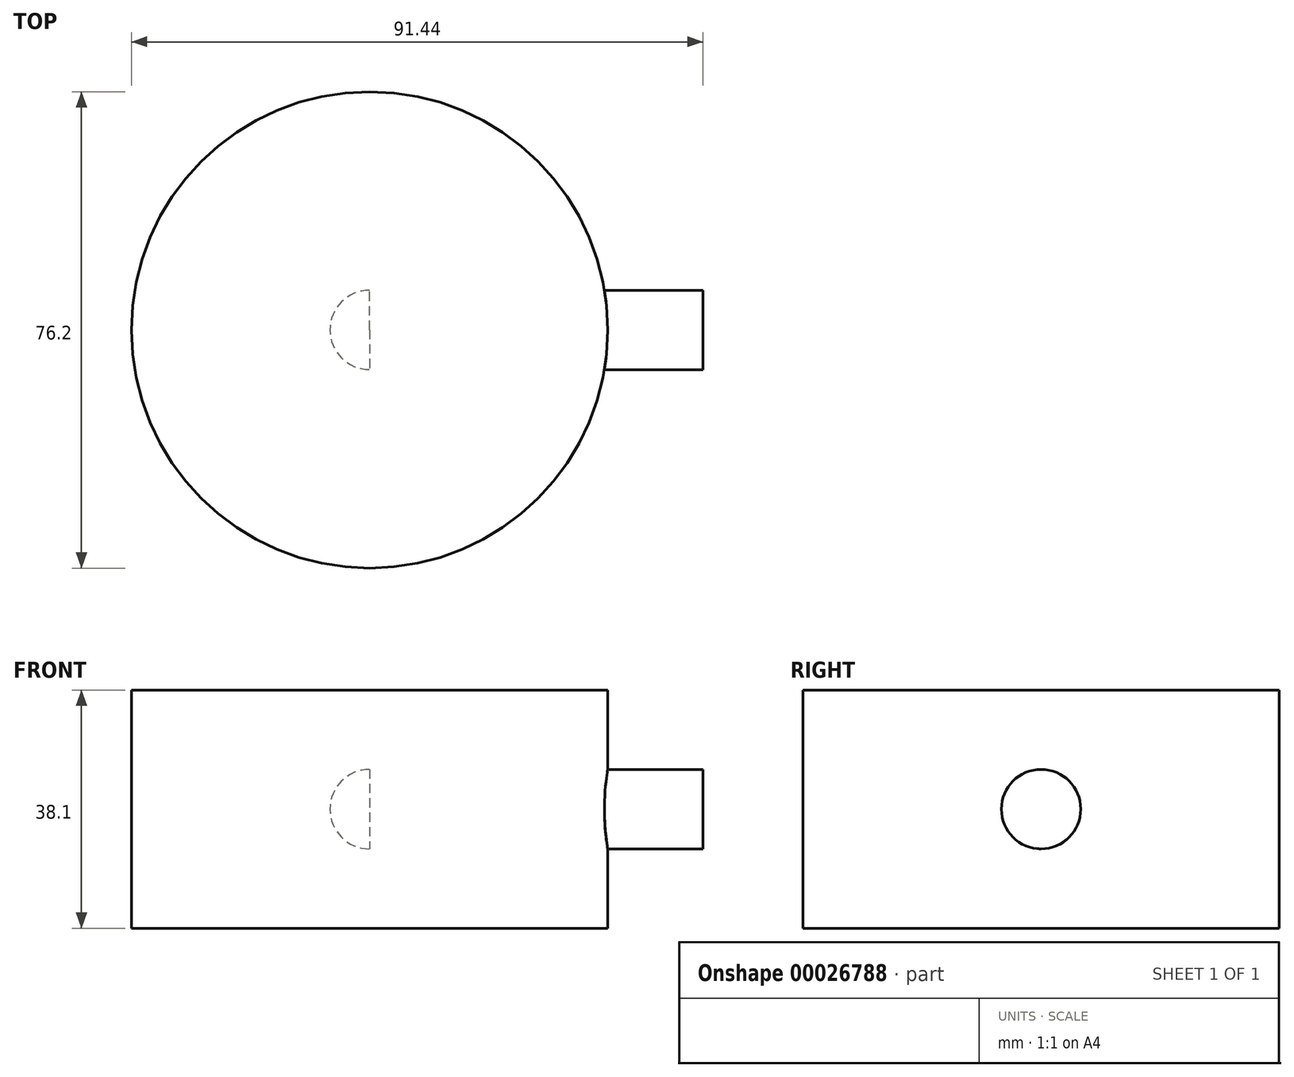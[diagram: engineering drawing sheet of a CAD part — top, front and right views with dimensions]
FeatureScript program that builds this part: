
annotation { "Feature Type Name" : "Feature", "Feature Type Description" : "" }
export const myFeature = defineFeature(function(context is Context, id is Id, definition is map)
    precondition{}
    {
        {
            var Q0;
            Q0=qCreatedBy(makeId("Right.planeOp"),FACE);
            var sketch = newSketch(context, id + "F0", { "sketchPlane" : qUnion([Q0])});
            skLineSegment(sketch, "E0.bottom", {"start": v(-23.4, 23.67) * mm, "end": v(14.7, 23.67) * mm});
            skLineSegment(sketch, "E0.top", {"start": v(-23.4, -14.43) * mm, "end": v(14.7, -14.43) * mm});
            skLineSegment(sketch, "E0.left", {"start": v(-23.4, 23.67) * mm, "end": v(-23.4, -14.43) * mm});
            skLineSegment(sketch, "E0.right", {"start": v(14.7, 23.67) * mm, "end": v(14.7, -14.43) * mm});
            skCircle(sketch, "E1", {"center": v(-23.4, 4.62) * mm, "radius": 6.35 * mm});
            skSolve(sketch);
        }
        {
            var Q0;
            {var subQ5=sQuery(id+"F0.wireOp",EDGE,"E0.bottom");Q0=makeQuery(id+"F0.imprint","IMPRINT",FACE,{"disambiguationData":[TD([[makeQuery(id+"F0.imprint","IMPRINT",EDGE,{"derivedFrom":subQ5}),-1.0]])]});}
            var Q1;
            Q1=sQuery(id+"F0.wireOp",EDGE,"E0.left");
            revolve(context, id + "F1", {"entities" : qUnion([Q0]), "axis" : qUnion([Q1]), "revolveType" : RevolveType.FULL});
        }
        {
            var Q0;
            {var subQ0=sQuery(id+"F0.wireOp",EDGE,"E1");var subQ1=sQuery(id+"F0.wireOp",EDGE,"E0.left");var subQ3=makeQuery(id+"F0.imprint","INTERSECT",VERTEX,{"disambiguationData":[OD(0.0)],"derivedFrom":[subQ1,subQ0]});Q0=makeQuery(id+"F0.imprint","IMPRINT",FACE,{"disambiguationData":[TD([[makeQuery(id+"F0.imprint","IMPRINT",EDGE,{"disambiguationData":[TD([[subQ3,-1.0]])],"derivedFrom":subQ1}),1.0]])]});}
            var Q1;
            {var subQ0=sQuery(id+"F0.wireOp",EDGE,"E1");var subQ1=sQuery(id+"F0.wireOp",EDGE,"E0.left");var subQ3=makeQuery(id+"F0.imprint","INTERSECT",VERTEX,{"disambiguationData":[OD(0.0)],"derivedFrom":[subQ1,subQ0]});Q1=makeQuery(id+"F0.imprint","IMPRINT",FACE,{"disambiguationData":[TD([[makeQuery(id+"F0.imprint","IMPRINT",EDGE,{"disambiguationData":[TD([[subQ3,-1.0]])],"derivedFrom":subQ1}),-1.0]])]});}
            extrude(context, id + "F2", {"entities" : qUnion([Q0, Q1]), "operationType" : NewBodyOperationType.ADD, "depth" : 53.34 * mm});
        }
    });
